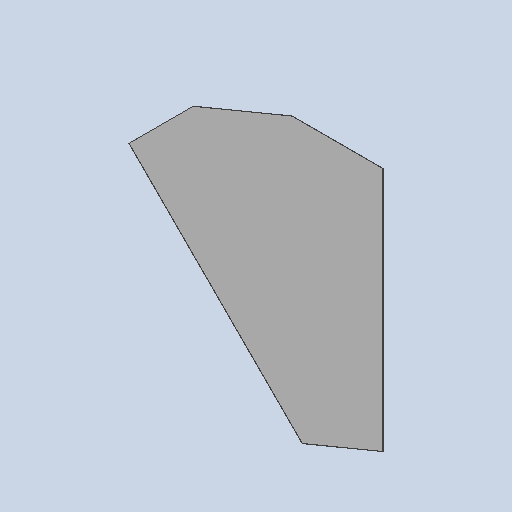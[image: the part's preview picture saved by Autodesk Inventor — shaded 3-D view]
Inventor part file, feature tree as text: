
AUTODESK INVENTOR PART (.ipt)
format: ipt  version: 2025 (Build 290162010, 162A)  size: 101,376 bytes
history: native  units: mm
features: other x3, sketch x1
ambient origin geometry x8: Origin, YZ Plane, XZ Plane, XY Plane, X Axis, Y Axis, Z Axis, Center Point
bodies: Solid1 (feature_tree)
feature tree (4):
  other  "ДМС 207 Сетка кассеты"
  other  "Solid1::ДМС 207 Сетка кассеты"
  other  "TaggingFeature1"
  sketch  "Sketch1"  dims[d0=10.0mm d1=0.5mm]
